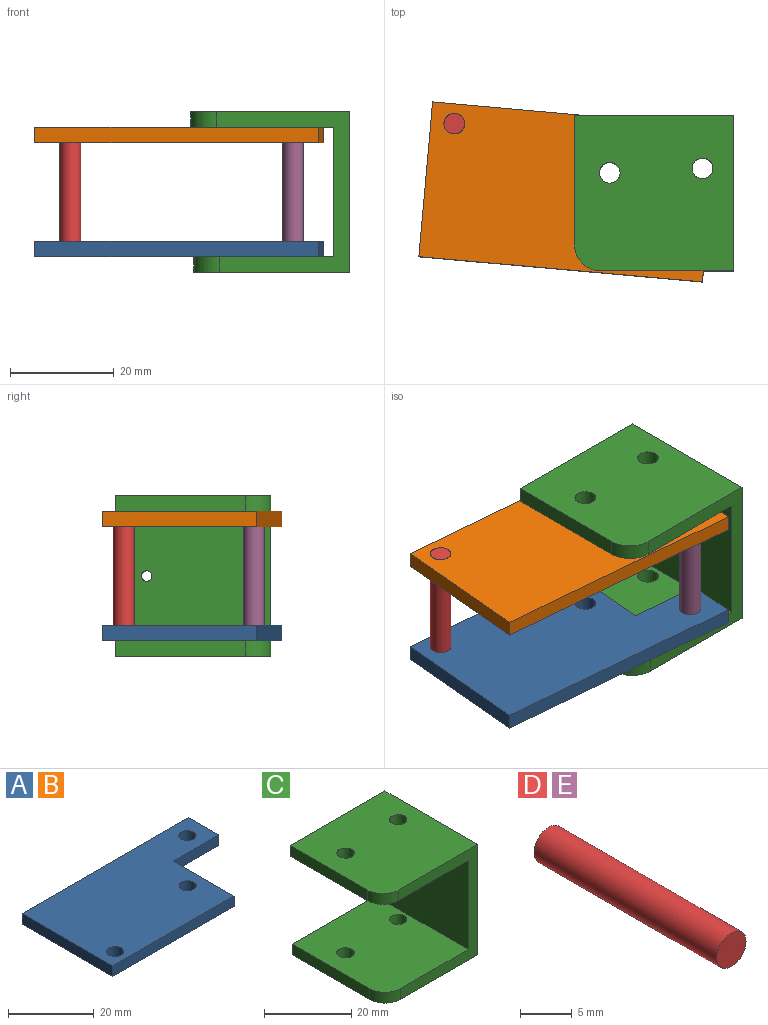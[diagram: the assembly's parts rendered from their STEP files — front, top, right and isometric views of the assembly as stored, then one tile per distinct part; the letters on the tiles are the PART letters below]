
ASSEMBLY  parts=5 mates=5
PART A: 11 faces, bbox 55x30x3 mm
  f0: plane 40x3mm, normal (0,-1,0), area 120mm2, adj f1,f5,f6,f7
  f1: plane 20x3mm, normal (1,0,0), area 60mm2, adj f0,f2,f6,f7
  f2: plane 15x3mm, normal (0,-1,0), area 45mm2, adj f1,f3,f6,f7
  f3: plane 10x3mm, normal (1,0,0), area 30mm2, adj f2,f4,f6,f7
  f4: plane 55x3mm, normal (0,1,0), area 165mm2, adj f3,f5,f6,f7
  f5: plane 30x3mm, normal (-1,0,0), area 90mm2, adj f0,f4,f6,f7
  f6: plane 55x30mm, normal (0,0,1), area 1312.3mm2, adj f0,f1,f2,f3,f4,f5,f8,f9
  f7: plane 55x30mm, normal (0,0,-1), area 1312.3mm2, adj f0,f1,f2,f3,f4,f5,f8,f9
  f8: cylinder r=2mm len=4mm, axis (0,0,1), area 37.7mm2, adj f6,f7
  f9: cylinder r=2mm len=4mm, axis (0,0,1), area 37.7mm2, adj f6,f7
  f10: cylinder r=2mm len=4mm, axis (0,0,1), area 37.7mm2, adj f6,f7
PART B: same geometry as A
PART C: 17 faces, bbox 30.6x30x31 mm
  f0: plane 30x27mm, normal (0,0,1), area 779.5mm2, adj f1,f7,f8,f9,f12,f14,f16
  f1: plane 25x3mm, normal (-1,0,0), area 75mm2, adj f0,f2,f9,f16
  f2: plane 30x30mm, normal (0,0,-1), area 869.5mm2, adj f1,f3,f8,f9,f12,f14,f16
  f3: plane 31x30mm, normal (1,0,0), area 926.9mm2, adj f2,f4,f8,f9,f10
  f4: plane 30.63x30mm, normal (0,0,1), area 888.5mm2, adj f3,f5,f8,f9,f11,f13,f15
  f5: plane 25x3mm, normal (-1,0,0), area 75mm2, adj f4,f6,f9,f15
  f6: plane 30x27.63mm, normal (0,0,-1), area 798.5mm2, adj f5,f7,f8,f9,f11,f13,f15
  f7: plane 30x25mm, normal (-1,0,0), area 746.9mm2, adj f0,f6,f8,f9,f10
  f8: plane 31x25.63mm, normal (0,-1,0), area 226.9mm2, adj f0,f2,f3,f4,f6,f7,f15,f16
  f9: plane 31x30.63mm, normal (0,1,0), area 256.9mm2, adj f0,f1,f2,f3,f4,f5,f6,f7
  f10: cylinder r=1mm len=3mm, axis (1,0,0), area 18.8mm2, adj f3,f7
  f11: cylinder r=2mm len=4mm, axis (0,0,-1), area 37.7mm2, adj f4,f6
  f12: cylinder r=2mm len=4mm, axis (0,0,-1), area 37.7mm2, adj f0,f2
  f13: cylinder r=2mm len=4mm, axis (0,0,-1), area 37.7mm2, adj f4,f6
  f14: cylinder r=2mm len=4mm, axis (0,0,-1), area 37.7mm2, adj f0,f2
  f15: cylinder r=5mm len=5mm, axis (0,0,1), area 23.6mm2, adj f4,f5,f6,f8
  f16: cylinder r=5mm len=5mm, axis (0,0,1), area 23.6mm2, adj f0,f1,f2,f8
PART D: 3 faces, bbox 4x25x4 mm
  f0: cylinder r=2mm len=25mm, axis (0,1,0), area 314.2mm2, adj f1,f2
  f1: plane 4x4mm, normal (0,-1,0), area 12.6mm2, adj f0
  f2: plane 4x4mm, normal (0,1,0), area 12.6mm2, adj f0
PART E: same geometry as D
PLACE A rot(axis=(1,-0.04,0),180deg) t=(-60.57,-52.1,-13.32)mm
PLACE B rot(axis=(-1,0.04,0),180deg) t=(-60.57,-52.1,8.68)mm
PLACE C t=(-54.4,-30,0.6)mm fixed
PLACE D rot(axis=(-0.06,0.71,-0.71),172.7deg) t=(-118.54,-41.29,-16.32)mm
PLACE E rot(axis=(-0.24,0.69,-0.69),152.9deg) t=(-69.13,-72.12,-16.32)mm
MATE revolute A.f8 <-> D.f0  axis (0,0,-1) through (-104.04,-31.56,-16.32)mm
MATE revolute B.f9 <-> C.f11  axis (0,0,1) through (-74.01,-41.05,8.68)mm
MATE revolute B.f8 <-> D.f0  axis (0,0,1) through (-104.04,-31.56,8.68)mm
MATE revolute A.f9 <-> C.f11  axis (0,0,-1) through (-74.01,-41.05,-16.32)mm
MATE revolute B.f10 <-> E.f0  axis (0,0,-1) through (-60.98,-56.67,8.68)mm
